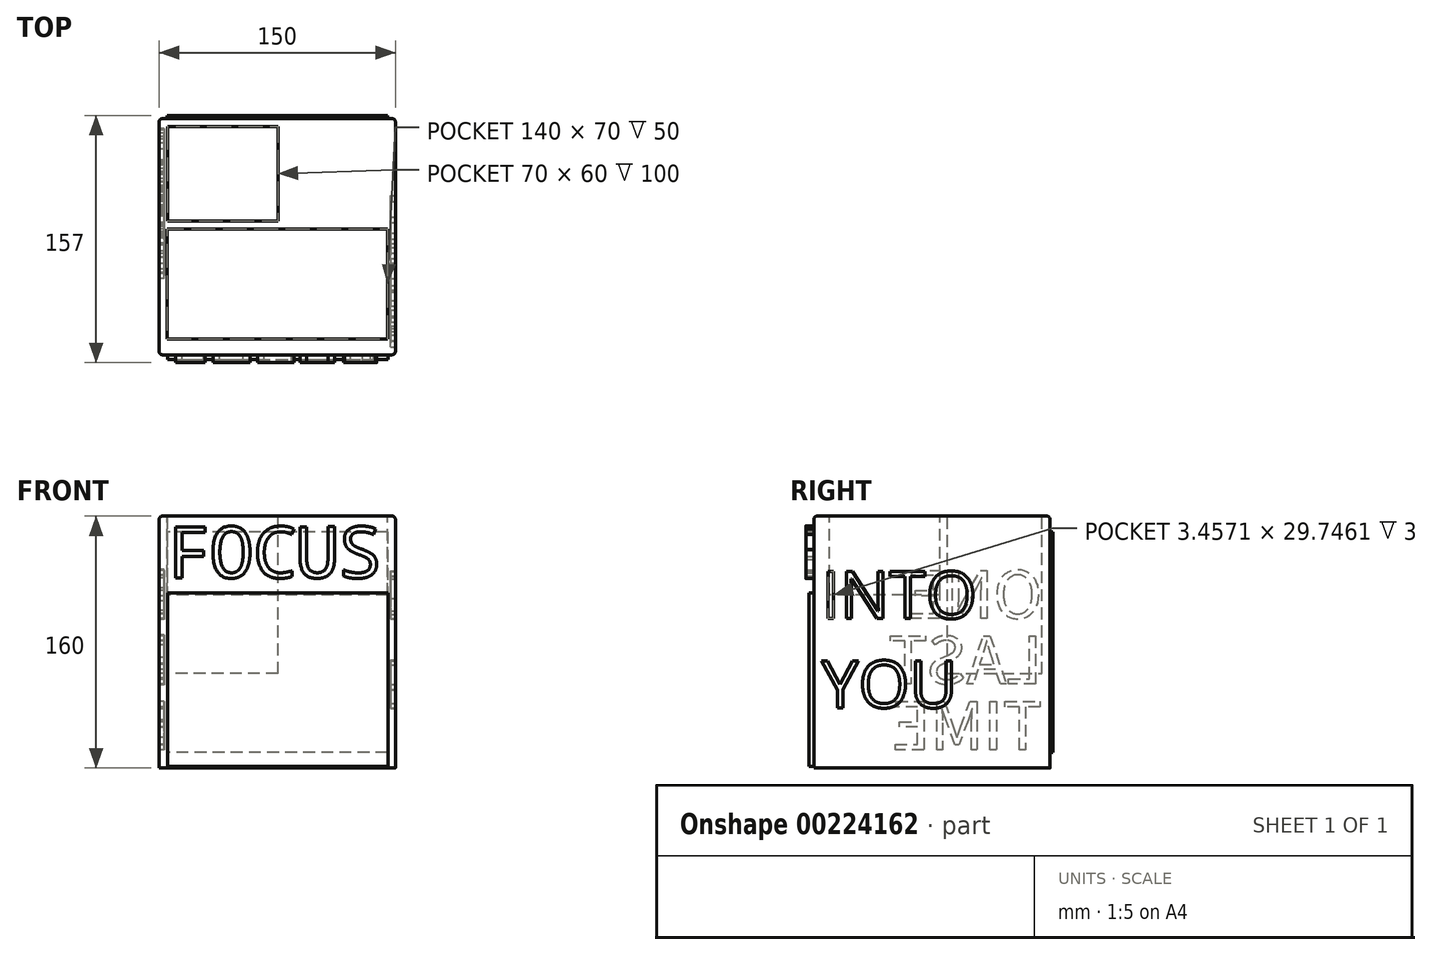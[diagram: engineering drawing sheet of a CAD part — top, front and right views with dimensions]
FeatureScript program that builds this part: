
annotation { "Feature Type Name" : "Feature", "Feature Type Description" : "" }
export const myFeature = defineFeature(function(context is Context, id is Id, definition is map)
    precondition{}
    {
        {
            var Q0;
            Q0=qCreatedBy(makeId("Front.planeOp"),FACE);
            var sketch = newSketch(context, id + "F0", { "sketchPlane" : qUnion([Q0])});
            skLineSegment(sketch, "E0.bottom", {"start": v(-75.44, 77.78) * mm, "end": v(74.56, 77.78) * mm});
            skLineSegment(sketch, "E0.top", {"start": v(-75.44, -82.22) * mm, "end": v(74.56, -82.22) * mm});
            skLineSegment(sketch, "E0.left", {"start": v(-75.44, 77.78) * mm, "end": v(-75.44, -82.22) * mm});
            skLineSegment(sketch, "E0.right", {"start": v(74.56, 77.78) * mm, "end": v(74.56, -82.22) * mm});
            skSolve(sketch);
        }
        {
            var Q0;
            Q0=makeQuery(id+"F0.imprint","IMPRINT",FACE,{"disambiguationData":[TD([[makeQuery(id+"F0.imprint","IMPRINT",EDGE,{"derivedFrom":sQuery(id+"F0.wireOp",EDGE,"E0.bottom")}),-1.0]])]});
            extrude(context, id + "F1", {"entities" : qUnion([Q0]), "depth" : 150 * mm});
        }
        {
            var Q0;
            Q0=makeQuery(id+"F1.opExtrude","SWEPT_FACE",FACE,{"disambiguationData":[OSD([sQuery(id+"F0.wireOp",EDGE,"E0.bottom")])]});
            var sketch = newSketch(context, id + "F2", { "sketchPlane" : qUnion([Q0])});
            skLineSegment(sketch, "E1.bottom", {"start": v(-75.44, 0) * mm, "end": v(74.56, 0) * mm});
            skLineSegment(sketch, "E1.top", {"start": v(-75.44, -150) * mm, "end": v(74.56, -150) * mm});
            skLineSegment(sketch, "E1.left", {"start": v(-75.44, 0) * mm, "end": v(-75.44, -150) * mm});
            skLineSegment(sketch, "E1.right", {"start": v(74.56, 0) * mm, "end": v(74.56, -150) * mm});
            skSolve(sketch);
        }
        {
            var Q0;
            Q0=makeQuery(id+"F2.imprint","IMPRINT",FACE,{"disambiguationData":[TD([[makeQuery(id+"F2.imprint","IMPRINT",EDGE,{"derivedFrom":sQuery(id+"F2.wireOp",EDGE,"E1.bottom")}),-1.0]])]});
            var sketch = newSketch(context, id + "F3", { "sketchPlane" : qUnion([Q0])});
            skLineSegment(sketch, "E2.bottom", {"start": v(74.76, -150.25) * mm, "end": v(-75.24, -150.25) * mm});
            skLineSegment(sketch, "E2.top", {"start": v(74.76, 0) * mm, "end": v(-75.24, 0) * mm});
            skLineSegment(sketch, "E2.left", {"start": v(74.76, -150.25) * mm, "end": v(74.76, 0) * mm});
            skLineSegment(sketch, "E2.right", {"start": v(-75.24, -150.25) * mm, "end": v(-75.24, 0) * mm});
            skSolve(sketch);
        }
        {
            var Q0;
            Q0=makeQuery(id+"F1.opExtrude","CAP_FACE",FACE,{"disambiguationData":[OSD([sQuery(id+"F0.wireOp",EDGE,"E0.bottom"),sQuery(id+"F0.wireOp",EDGE,"E0.top"),sQuery(id+"F0.wireOp",EDGE,"E0.left"),sQuery(id+"F0.wireOp",EDGE,"E0.right")])],"isStart":false});
            var sketch = newSketch(context, id + "F4", { "sketchPlane" : qUnion([Q0])});
            skText(sketch, "E3", { "text": "FOCUS", "fontName": "DroidSansMono.ttf"});
            const initialGuessF4  = {"E3": [-0.07044, 0.03862, 1, 0, 0.03271]};
            skSetInitialGuess(sketch, initialGuessF4);
            skSolve(sketch);
        }
        {
            var Q0;
            Q0 = qSketchRegion(id + "F4", true);
            extrude(context, id + "F5", {"entities" : qUnion([Q0]), "operationType" : NewBodyOperationType.ADD, "depth" : 5 * mm});
        }
        {
            var Q0;
            {var subQ0=sQuery(id+"F0.wireOp",EDGE,"E0.right");Q0=makeQuery(id+"FR0FVllD1I36URP_1.boolean.opBoolean","MERGE",FACE,{"derivedFrom":[makeQuery(id+"F1.opExtrude","CAP_FACE",FACE,{"disambiguationData":[OSD([sQuery(id+"F0.wireOp",EDGE,"E0.bottom"),sQuery(id+"F0.wireOp",EDGE,"E0.top"),sQuery(id+"F0.wireOp",EDGE,"E0.left"),subQ0])],"isStart":true}),makeQuery(id+"FR0FVllD1I36URP_1.opExtrude","SWEPT_FACE",FACE,{"disambiguationData":[OSD([subQ0]),TDD([makeQuery(id+"FywjjdvTAaoKOOV_1.imprint","IMPRINT",EDGE,{"derivedFrom":makeQuery(id+"F1.opExtrude","CAP_EDGE",EDGE,{"disambiguationData":[OSD([subQ0])],"isStart":true})})])]})]});}
            var sketch = newSketch(context, id + "F6", { "sketchPlane" : qUnion([Q0])});
            skLineSegment(sketch, "E4.bottom", {"start": v(-69.56, 67.78) * mm, "end": v(70.44, 67.78) * mm});
            skLineSegment(sketch, "E4.top", {"start": v(-69.56, -72.22) * mm, "end": v(70.44, -72.22) * mm});
            skLineSegment(sketch, "E4.left", {"start": v(-69.56, 67.78) * mm, "end": v(-69.56, -72.22) * mm});
            skLineSegment(sketch, "E4.right", {"start": v(70.44, 67.78) * mm, "end": v(70.44, -72.22) * mm});
            skSolve(sketch);
        }
        {
            var Q0;
            Q0=makeQuery(id+"F6.imprint","IMPRINT",FACE,{"disambiguationData":[TD([[makeQuery(id+"F6.imprint","IMPRINT",EDGE,{"derivedFrom":sQuery(id+"F6.wireOp",EDGE,"E4.bottom")}),-1.0]])]});
            extrude(context, id + "F7", {"entities" : qUnion([Q0]), "operationType" : NewBodyOperationType.ADD, "depth" : 2 * mm});
        }
        {
            var Q0;
            Q0=makeQuery(id+"F1.opExtrude","SWEPT_FACE",FACE,{"disambiguationData":[OSD([sQuery(id+"F0.wireOp",EDGE,"E0.left")])]});
            var sketch = newSketch(context, id + "F8", { "sketchPlane" : qUnion([Q0])});
            skText(sketch, "E5", { "text": "ONE \nLAST\nTIME", "fontName": "NotoSansCJKjp-Regular.otf"});
            const initialGuessF8  = {"E5": [0.005, 0.01278, 1, 0, 0.03]};
            skSetInitialGuess(sketch, initialGuessF8);
            skSolve(sketch);
        }
        {
            var Q0;
            Q0 = qSketchRegion(id + "F8", true);
            extrude(context, id + "F9", {"entities" : qUnion([Q0]), "operationType" : NewBodyOperationType.REMOVE, "oppositeDirection" : true, "depth" : 3 * mm});
        }
        {
            var Q0;
            Q0=makeQuery(id+"F1.opExtrude","SWEPT_FACE",FACE,{"disambiguationData":[OSD([sQuery(id+"F0.wireOp",EDGE,"E0.right")])]});
            var sketch = newSketch(context, id + "F10", { "sketchPlane" : qUnion([Q0])});
            skText(sketch, "E6", { "text": "INTO\nYOU", "fontName": "OpenSans-Regular.ttf"});
            const initialGuessF10  = {"E6": [-0.145, 0.01278, 1, 0, 0.03]};
            skSetInitialGuess(sketch, initialGuessF10);
            skSolve(sketch);
        }
        {
            var Q0;
            Q0 = qSketchRegion(id + "F10", true);
            extrude(context, id + "F11", {"entities" : qUnion([Q0]), "operationType" : NewBodyOperationType.REMOVE, "oppositeDirection" : true, "depth" : 3 * mm});
        }
        {
            var Q0;
            {var subQ1=makeQuery(id+"F2.imprint","IMPRINT",EDGE,{"derivedFrom":sQuery(id+"F2.wireOp",EDGE,"E1.right")});Q0=makeQuery(id+"F3.imprint","IMPRINT",FACE,{"disambiguationData":[TD([[makeQuery(id+"F3.imprint","IMPRINT",EDGE,{"derivedFrom":subQ1}),1.0]])]});}
            var sketch = newSketch(context, id + "F12", { "sketchPlane" : qUnion([Q0])});
            skLineSegment(sketch, "E7.bottom", {"start": v(69.76, -70) * mm, "end": v(-70.24, -70) * mm});
            skLineSegment(sketch, "E7.top", {"start": v(69.76, -140) * mm, "end": v(-70.24, -140) * mm});
            skLineSegment(sketch, "E7.left", {"start": v(69.76, -70) * mm, "end": v(69.76, -140) * mm});
            skLineSegment(sketch, "E7.right", {"start": v(-70.24, -70) * mm, "end": v(-70.24, -140) * mm});
            skSolve(sketch);
        }
        {
            var Q0;
            Q0=makeQuery(id+"F1.opExtrude","SWEPT_EDGE",EDGE,{"disambiguationData":[OSD([sQuery(id+"F0.wireOp",EDGE,"E0.bottom"),sQuery(id+"F0.wireOp",EDGE,"E0.right")])]});
            var Q1;
            Q1=makeQuery(id+"F1.opExtrude","CAP_EDGE",EDGE,{"disambiguationData":[OSD([sQuery(id+"F0.wireOp",EDGE,"E0.bottom")])],"isStart":false});
            var Q2;
            Q2=makeQuery(id+"F1.opExtrude","CAP_EDGE",EDGE,{"disambiguationData":[OSD([sQuery(id+"F0.wireOp",EDGE,"E0.bottom")])],"isStart":true});
            var Q3;
            Q3=makeQuery(id+"F1.opExtrude","SWEPT_EDGE",EDGE,{"disambiguationData":[OSD([sQuery(id+"F0.wireOp",EDGE,"E0.bottom"),sQuery(id+"F0.wireOp",EDGE,"E0.left")])]});
            var Q4;
            Q4=makeQuery(id+"F1.opExtrude","CAP_EDGE",EDGE,{"disambiguationData":[OSD([sQuery(id+"F0.wireOp",EDGE,"E0.right")])],"isStart":true});
            var Q5;
            Q5=makeQuery(id+"F1.opExtrude","CAP_EDGE",EDGE,{"disambiguationData":[OSD([sQuery(id+"F0.wireOp",EDGE,"E0.right")])],"isStart":false});
            var Q6;
            Q6=makeQuery(id+"F1.opExtrude","CAP_EDGE",EDGE,{"disambiguationData":[OSD([sQuery(id+"F0.wireOp",EDGE,"E0.left")])],"isStart":false});
            var Q7;
            Q7=makeQuery(id+"F1.opExtrude","CAP_EDGE",EDGE,{"disambiguationData":[OSD([sQuery(id+"F0.wireOp",EDGE,"E0.left")])],"isStart":true});
            fillet(context, id + "F13", {"entities" : qUnion([Q0, Q1, Q2, Q3, Q4, Q5, Q6, Q7]), "radius" : 2 * mm, "tangentPropagation" : true, "allowEdgeOverflow" : false});
        }
        {
            var Q0;
            Q0=makeQuery(id+"F12.imprint","IMPRINT",FACE,{"disambiguationData":[TD([[makeQuery(id+"F12.imprint","IMPRINT",EDGE,{"derivedFrom":sQuery(id+"F12.wireOp",EDGE,"E7.bottom")}),1.0]])]});
            extrude(context, id + "F14", {"entities" : qUnion([Q0]), "operationType" : NewBodyOperationType.REMOVE, "oppositeDirection" : true, "depth" : 50 * mm});
        }
        {
            var Q0;
            Q0=makeQuery(id+"F2.imprint","IMPRINT",FACE,{"disambiguationData":[TD([[makeQuery(id+"F2.imprint","IMPRINT",EDGE,{"derivedFrom":sQuery(id+"F2.wireOp",EDGE,"E1.bottom")}),-1.0]])]});
            var sketch = newSketch(context, id + "F15", { "sketchPlane" : qUnion([Q0])});
            skLineSegment(sketch, "E8.bottom", {"start": v(0, -65) * mm, "end": v(-70, -65) * mm});
            skLineSegment(sketch, "E8.top", {"start": v(0, -5) * mm, "end": v(-70, -5) * mm});
            skLineSegment(sketch, "E8.left", {"start": v(0, -65) * mm, "end": v(0, -5) * mm});
            skLineSegment(sketch, "E8.right", {"start": v(-70, -65) * mm, "end": v(-70, -5) * mm});
            skSolve(sketch);
        }
        {
            var Q0;
            Q0=makeQuery(id+"F15.imprint","IMPRINT",FACE,{"disambiguationData":[TD([[makeQuery(id+"F15.imprint","IMPRINT",EDGE,{"derivedFrom":sQuery(id+"F15.wireOp",EDGE,"E8.bottom")}),-1.0]])]});
            extrude(context, id + "F16", {"entities" : qUnion([Q0]), "operationType" : NewBodyOperationType.REMOVE, "oppositeDirection" : true, "depth" : 100 * mm});
        }
        {
            var Q0;
            {var subQ0=sQuery(id+"F0.wireOp",EDGE,"E0.top");var subQ1=sQuery(id+"F0.wireOp",EDGE,"E0.bottom");var subQ2=sQuery(id+"F0.wireOp",EDGE,"E0.left");var subQ3=sQuery(id+"F0.wireOp",EDGE,"E0.right");Q0=makeQuery(id+"F5.boolean.opBoolean","SPLIT",FACE,{"disambiguationData":[TD([makeQuery(id+"F1.opExtrude","SWEPT_FACE",FACE,{"disambiguationData":[OSD([subQ1])]})])],"derivedFrom":makeQuery(id+"F1.opExtrude","CAP_FACE",FACE,{"disambiguationData":[OSD([subQ1,subQ0,subQ2,subQ3])],"isStart":false})});}
            var sketch = newSketch(context, id + "F17", { "sketchPlane" : qUnion([Q0])});
            skLineSegment(sketch, "E9.bottom", {"start": v(-69.94, 28.9) * mm, "end": v(70.06, 28.9) * mm});
            skLineSegment(sketch, "E9.top", {"start": v(-69.94, -81.1) * mm, "end": v(70.06, -81.1) * mm});
            skLineSegment(sketch, "E9.left", {"start": v(-69.94, 28.9) * mm, "end": v(-69.94, -81.1) * mm});
            skLineSegment(sketch, "E9.right", {"start": v(70.06, 28.9) * mm, "end": v(70.06, -81.1) * mm});
            skSolve(sketch);
        }
        {
            var Q0;
            Q0=makeQuery(id+"F17.imprint","IMPRINT",FACE,{"disambiguationData":[TD([[makeQuery(id+"F17.imprint","IMPRINT",EDGE,{"derivedFrom":sQuery(id+"F17.wireOp",EDGE,"E9.bottom")}),-1.0]])]});
            extrude(context, id + "F18", {"entities" : qUnion([Q0]), "operationType" : NewBodyOperationType.ADD, "depth" : 3 * mm});
        }
    });
